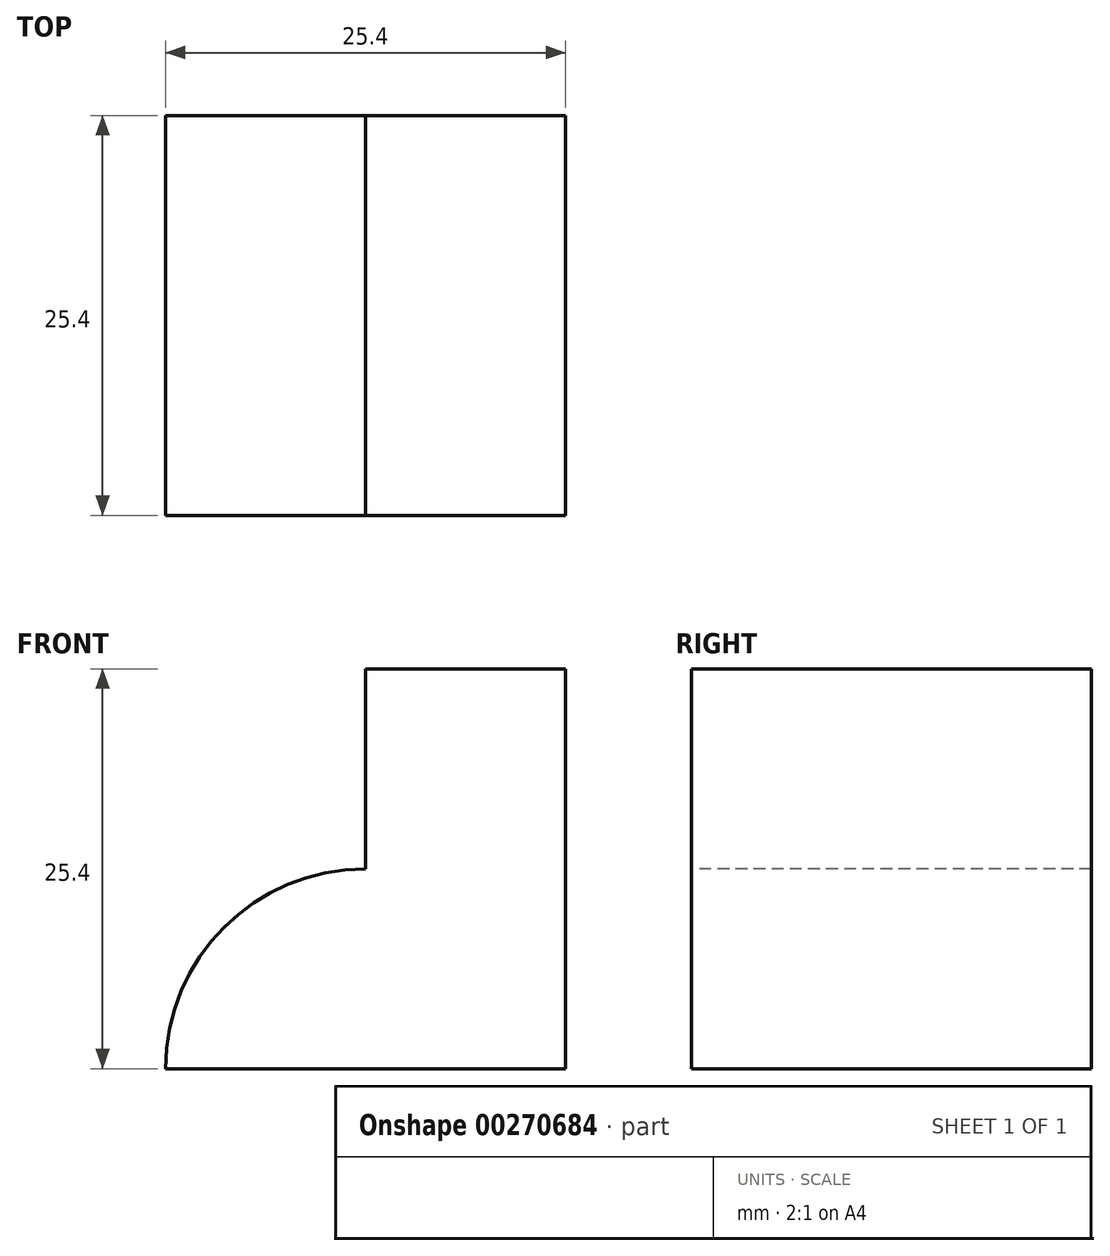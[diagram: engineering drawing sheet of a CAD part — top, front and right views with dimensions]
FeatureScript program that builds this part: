
annotation { "Feature Type Name" : "Feature", "Feature Type Description" : "" }
export const myFeature = defineFeature(function(context is Context, id is Id, definition is map)
    precondition{}
    {
        {
            var Q0;
            Q0=qCreatedBy(makeId("Front.planeOp"),FACE);
            var sketch = newSketch(context, id + "F0", { "sketchPlane" : qUnion([Q0])});
            skLineSegment(sketch, "E0.bottom", {"start": v(0, 0) * mm, "end": v(-25.4, 0) * mm});
            skLineSegment(sketch, "E0.top", {"start": v(0, 25.4) * mm, "end": v(-25.4, 25.4) * mm});
            skLineSegment(sketch, "E0.left", {"start": v(0, 0) * mm, "end": v(0, 25.4) * mm});
            skLineSegment(sketch, "E0.right", {"start": v(-25.4, 0) * mm, "end": v(-25.4, 25.4) * mm});
            skSolve(sketch);
        }
        {
            var Q0;
            Q0=makeQuery(id+"F0.imprint","IMPRINT",FACE,{"disambiguationData":[TD([[makeQuery(id+"F0.imprint","IMPRINT",EDGE,{"derivedFrom":sQuery(id+"F0.wireOp",EDGE,"E0.bottom")}),-1.0]])]});
            extrude(context, id + "F1", {"entities" : qUnion([Q0]), "depth" : 25.4 * mm});
        }
        {
            var Q0;
            Q0=makeQuery(id+"F1.opExtrude","CAP_FACE",FACE,{"disambiguationData":[OSD([sQuery(id+"F0.wireOp",EDGE,"E0.bottom"),sQuery(id+"F0.wireOp",EDGE,"E0.top"),sQuery(id+"F0.wireOp",EDGE,"E0.left"),sQuery(id+"F0.wireOp",EDGE,"E0.right")])],"isStart":false});
            var sketch = newSketch(context, id + "F2", { "sketchPlane" : qUnion([Q0])});
            skLineSegment(sketch, "E1", {"start": v(-12.7, 25.4) * mm, "end": v(-12.7, 12.7) * mm});
            skPoint(sketch, "E1.endSnap0", {"position": v(-25.4, 12.7) * mm});
            skLineSegment(sketch, "E2", {"start": v(-12.7, 12.7) * mm, "end": v(-25.4, 12.7) * mm});
            skSolve(sketch);
        }
        {
            var Q0;
            {var subQ0=sQuery(id+"F2.wireOp",EDGE,"E1");Q0=makeQuery(id+"F2.imprint","IMPRINT",FACE,{"disambiguationData":[TD([[makeQuery(id+"F2.imprint","IMPRINT",EDGE,{"derivedFrom":subQ0}),-1.0]])]});}
            extrude(context, id + "F3", {"entities" : qUnion([Q0]), "operationType" : NewBodyOperationType.REMOVE, "oppositeDirection" : true, "depth" : 25.4 * mm});
        }
        {
            var Q0;
            Q0=makeQuery(id+"F1.opExtrude","CAP_FACE",FACE,{"disambiguationData":[OSD([sQuery(id+"F0.wireOp",EDGE,"E0.bottom"),sQuery(id+"F0.wireOp",EDGE,"E0.top"),sQuery(id+"F0.wireOp",EDGE,"E0.left"),sQuery(id+"F0.wireOp",EDGE,"E0.right")])],"isStart":false});
            var sketch = newSketch(context, id + "F4", { "sketchPlane" : qUnion([Q0])});
            skArc(sketch, "E3", {"start": v(-12.7, 12.7) * mm, "mid": v(-21.68, 8.98) * mm, "end": v(-25.4, 0) * mm});
            skSolve(sketch);
        }
        {
            var Q0;
            Q0=makeQuery(id+"F4.imprint","IMPRINT",FACE,{"disambiguationData":[TD([[makeQuery(id+"F4.imprint","IMPRINT",EDGE,{"derivedFrom":sQuery(id+"F4.wireOp",EDGE,"E3")}),-1.0]])]});
            extrude(context, id + "F5", {"entities" : qUnion([Q0]), "operationType" : NewBodyOperationType.REMOVE, "oppositeDirection" : true, "depth" : 25.4 * mm});
        }
    });
